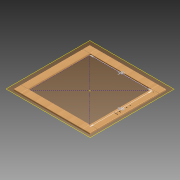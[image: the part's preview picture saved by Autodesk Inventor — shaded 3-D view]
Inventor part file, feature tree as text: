
AUTODESK INVENTOR PART (.ipt)
format: ipt  version: 2013 SP1 (Build 170176100, 176)  size: 304,128 bytes
history: native  units: mm
features: chamfer x19, sketch x7, extrude x3, mirror x2, hole x2, pattern_linear x1, plane x1
ambient origin geometry x8: Origin, YZ Plane, XZ Plane, XY Plane, X Axis, Y Axis, Z Axis, Center Point
bodies: Volumenkörper2 (feature_tree), Volumenkörper3 (feature_tree), Volumenkörper5 (feature_tree)
feature tree (35):
  sketch  "Skizze Helper"  dims[d19=40.0mm d20=9.0mm d21=0.0mm d24=20.0mm d26=380.0mm d27=20.0mm d29=380.0mm d34=1.0mm d35=2.0mm d36=45.0deg d37=1.0mm d38=2.0mm d39=45.0deg d40=1.0mm d41=2.0mm d42=45.0deg d43=1.0mm d44=2.0mm d45=45.0deg d46=1.0mm d47=2.0mm d48=45.0deg d49=1.0mm d50=2.0mm d51=45.0deg d52=1.0mm d53=2.0mm d54=45.0deg d55=1.0mm d56=2.0mm d57=45.0deg d58=1.0mm d59=2.0mm d60=45.0deg d61=1.0mm d62=2.0mm d63=45.0deg d64=1.0mm d65=2.0mm d66=45.0deg d67=1.0mm d68=2.0mm d69=45.0deg d70=1.0mm d71=2.0mm d72=45.0deg d73=1.0mm d74=2.0mm d75=45.0deg d76=1.0mm d77=2.0mm d78=45.0deg]
  extrude  "Extrusion3"  Depth=340.0mm
  extrude  "Extrusion4"  Depth=340.0mm
  mirror  "Spiegeln1"
  mirror  "Spiegeln2"
  extrude  "Extrusion5"  Depth=340.0mm
  pattern_linear  "Rechteckige Anordnung1"  Count1=4  [1 undecoded]
  chamfer  "Fase1"  Distance=9.0mm
  chamfer  "Fase2"  Distance=9.0mm
  chamfer  "Fase3"  Distance=20.0mm
  chamfer  "Fase4"  Distance=20.0mm
  chamfer  "Fase5"  Distance=1.0mm Angle=45.0deg
  chamfer  "Fase6"  Distance=1.0mm Angle=45.0deg
  chamfer  "Fase7"  Distance=1.0mm Angle=45.0deg
  chamfer  "Fase8"  Distance=1.0mm Angle=45.0deg
  chamfer  "Fase9"  Distance=1.0mm Angle=45.0deg
  chamfer  "Fase10"  Distance=1.0mm Angle=45.0deg
  chamfer  "Fase11"  Distance=1.0mm Angle=45.0deg
  chamfer  "Fase12"  Distance=1.0mm Angle=45.0deg
  chamfer  "Fase13"  Distance=1.0mm Angle=45.0deg
  chamfer  "Fase14"  Distance=1.0mm Angle=45.0deg
  chamfer  "Fase15"  Distance=1.0mm Angle=45.0deg
  chamfer  "Fase16"  Distance=1.0mm Angle=45.0deg
  chamfer  "Fase17"  Distance=1.0mm Angle=45.0deg
  chamfer  "Fase18"  Distance=1.0mm Angle=45.0deg
  chamfer  "Fase19"  Distance=1.0mm Angle=45.0deg
  plane  "Arbeitsebene3"
  hole  "Bohrung 6mm"  [1 undecoded]
  hole  "Bohrung 5mm"  [1 undecoded]
  sketch  "Skizze Beschriftung"  dims[d79=1.0mm d80=2.0mm d81=45.0deg d82=1.0mm d83=2.0mm d84=45.0deg]
  sketch  "Skizze4"  dims[d0=340.0mm d1=340.0mm]
  sketch  "Skizze5"  dims[d10=40.0mm d11=340.0mm]
  sketch  "Skizze7"  dims[d12=9.0mm d13=0.0mm d14=340.0mm d15=40.0mm d16=9.0mm d17=0.0mm]
  sketch  "Skizze Bohrung"  dims[d85=1.0mm d86=2.0mm d87=45.0deg d88=1.0mm d89=2.0mm d90=45.0deg d104=6.0mm d105=6.0mm d106=4.0mm d107=2.0mm d108=90.0deg d109=6.0mm d110=20.594885mm d111=6.0mm d114=5.0mm d115=5.0mm d116=5.0mm d117=6.0mm d118=4.0mm d119=2.0mm d120=90.0deg d121=6.0mm d122=20.594885mm d126=9.0mm d100=1.0mm d101=1.0mm d103=1.0mm]
  sketch  "Skizze10"  dims[d18=40.0mm]
note: 3 required parameter values undecoded (feature->parameter linkage not recoverable at this tier; creation-order binding heuristic only, values carry confidence <= 0.55)
